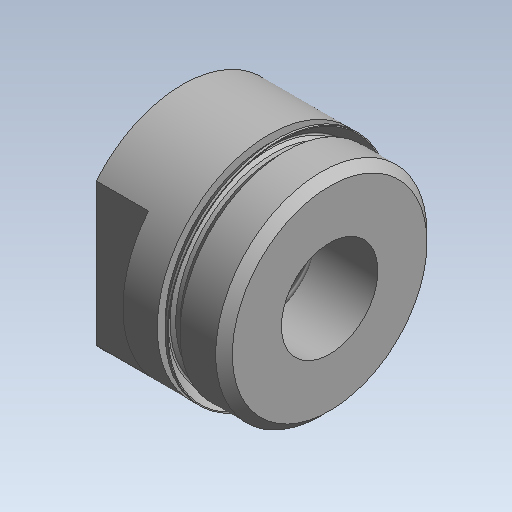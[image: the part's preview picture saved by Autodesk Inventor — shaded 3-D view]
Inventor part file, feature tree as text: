
AUTODESK INVENTOR PART (.ipt)
format: ipt  version: 2020 (Build 240168000, 168)  size: 228,352 bytes
history: native  units: mm (DEFAULTED — no unit token found)
features: other x126, sketch x4, revolve x3, thread x1, extrude x1
ambient origin geometry x8: Origin, YZ Plane, XZ Plane, XY Plane, X Axis, Y Axis, Z Axis, Center Point
bodies: Solid1 (feature_tree)
feature tree (135):
  revolve  "Revolution1"  Angle=360.0deg
  revolve  "Revolution2"  [1 undecoded]
  thread  "Thread1"  [1 undecoded]
  extrude  "Extrusion1"  [1 undecoded]
  revolve  "Revolution3"  [1 undecoded]
  other  "cut1_XY"
  other  "cut1_YZ"
  other  "cut1_ZX"
  other  "cut1_X"
  other  "cut1_Y"
  other  "cut1_Z"
  other  "cut1_Center"
  other  "cut2_XY"
  other  "cut2_YZ"
  other  "cut2_ZX"
  other  "cut2_X"
  other  "cut2_Y"
  other  "cut2_Z"
  other  "cut2_Center"
  other  "cutf1_XY"
  other  "cutf1_YZ"
  other  "cutf1_ZX"
  other  "cutf1_X"
  other  "cutf1_Y"
  other  "cutf1_Z"
  other  "cutf1_Center"
  other  "cutf2_XY"
  other  "cutf2_YZ"
  other  "cutf2_ZX"
  other  "cutf2_X"
  other  "cutf2_Y"
  other  "cutf2_Z"
  other  "cutf2_Center"
  other  "lovra_XY"
  other  "lovra_YZ"
  other  "lovra_ZX"
  other  "lovra_X"
  other  "lovra_Y"
  other  "lovra_Z"
  other  "lovra_Center"
  other  "lovra1_XY"
  other  "lovra1_YZ"
  other  "lovra1_ZX"
  other  "lovra1_X"
  other  "lovra1_Y"
  other  "lovra1_Z"
  other  "lovra1_Center"
  other  "lovra2_XY"
  other  "lovra2_YZ"
  other  "lovra2_ZX"
  other  "lovra2_X"
  other  "lovra2_Y"
  other  "lovra2_Z"
  other  "lovra2_Center"
  other  "lovra21_XY"
  other  "lovra21_YZ"
  other  "lovra21_ZX"
  other  "lovra21_X"
  other  "lovra21_Y"
  other  "lovra21_Z"
  other  "lovra21_Center"
  other  "lovra22_XY"
  other  "lovra22_YZ"
  other  "lovra22_ZX"
  other  "lovra22_X"
  other  "lovra22_Y"
  other  "lovra22_Z"
  other  "lovra22_Center"
  other  "lovra3_XY"
  other  "lovra3_YZ"
  other  "lovra3_ZX"
  other  "lovra3_X"
  other  "lovra3_Y"
  other  "lovra3_Z"
  other  "lovra3_Center"
  other  "olen_XY"
  other  "olen_YZ"
  other  "olen_ZX"
  other  "olen_X"
  other  "olen_Y"
  other  "olen_Z"
  other  "olen_Center"
  other  "to_mounting_bracket_XY"
  other  "to_mounting_bracket_YZ"
  other  "to_mounting_bracket_ZX"
  other  "to_mounting_bracket_X"
  other  "to_mounting_bracket_Y"
  other  "to_mounting_bracket_Z"
  other  "to_mounting_bracket_Center"
  other  "to_nut_XY"
  other  "to_nut_YZ"
  other  "to_nut_ZX"
  other  "to_nut_X"
  other  "to_nut_Y"
  other  "to_nut_Z"
  other  "to_nut_Center"
  other  "to_pin_XY"
  other  "to_pin_YZ"
  other  "to_pin_ZX"
  other  "to_pin_X"
  other  "to_pin_Y"
  other  "to_pin_Z"
  other  "to_pin_Center"
  other  "to_pin_1_XY"
  other  "to_pin_1_YZ"
  other  "to_pin_1_ZX"
  other  "to_pin_1_X"
  other  "to_pin_1_Y"
  other  "to_pin_1_Z"
  other  "to_pin_1_Center"
  other  "to_pin_r_XY"
  other  "to_pin_r_YZ"
  other  "to_pin_r_ZX"
  other  "to_pin_r_X"
  other  "to_pin_r_Y"
  other  "to_pin_r_Z"
  other  "to_pin_r_Center"
  other  "to_screw_XY"
  other  "to_screw_YZ"
  other  "to_screw_ZX"
  other  "to_screw_X"
  other  "to_screw_Y"
  other  "to_screw_Z"
  other  "to_screw_Center"
  other  "to_tube_XY"
  other  "to_tube_YZ"
  other  "to_tube_ZX"
  other  "to_tube_X"
  other  "to_tube_Y"
  other  "to_tube_Z"
  other  "to_tube_Center"
  sketch  "Sketch_1"  dims[d0=360.0deg d1=360.0deg]
  sketch  "Sketch_6"  dims[d7=0.0mm d8=0.0mm d9=0.0mm d10=0.0mm d11=0.0mm d12=0.0mm d13=0.0mm d14=0.0mm d15=0.0mm d16=0.0mm]
  sketch  "Sketch_5"  dims[d2=7.03922mm d3=0.0mm d4=4.7752mm d5=0.0mm d6=360.0deg]
  sketch  "Sketch_24"
note: 4 required parameter values undecoded (feature->parameter linkage not recoverable at this tier; creation-order binding heuristic only, values carry confidence <= 0.55)